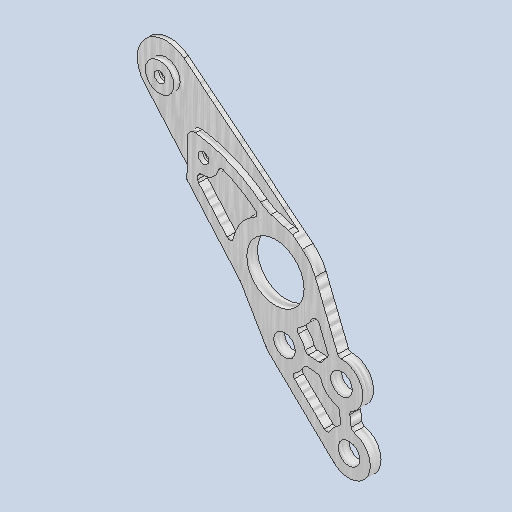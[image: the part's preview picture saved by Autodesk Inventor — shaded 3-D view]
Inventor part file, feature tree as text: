
AUTODESK INVENTOR PART (.ipt)
format: ipt  version: 2023 (Build 270158030, 158C)  size: 436,736 bytes
history: native  units: mm
features: extrude x4, other x2, sketch x2, hole x1, chamfer x1
ambient origin geometry x8: Origin, YZ Plane, XZ Plane, XY Plane, X Axis, Y Axis, Z Axis, Center Point
bodies: Body1 (feature_tree)
feature tree (10):
  other  "ソリッド1"
  sketch  "スケッチ1"
  extrude  "押し出し1"  Depth=3.0mm TaperAngle=0.0deg
  extrude  "押し出し2"  Depth=2.0mm TaperAngle=0.0deg
  extrude  "押し出し3"  Depth=2.5mm TaperAngle=0.0deg
  hole  "穴1"  [1 undecoded]
  extrude  "押し出し4"  Depth=1.75mm TaperAngle=45.0deg
  chamfer  "面取り1"  [1 undecoded]
  sketch  "スケッチ2"
  other  "断面エッジを投影1"
note: 2 required parameter values undecoded (feature->parameter linkage not recoverable at this tier; creation-order binding heuristic only, values carry confidence <= 0.55)
